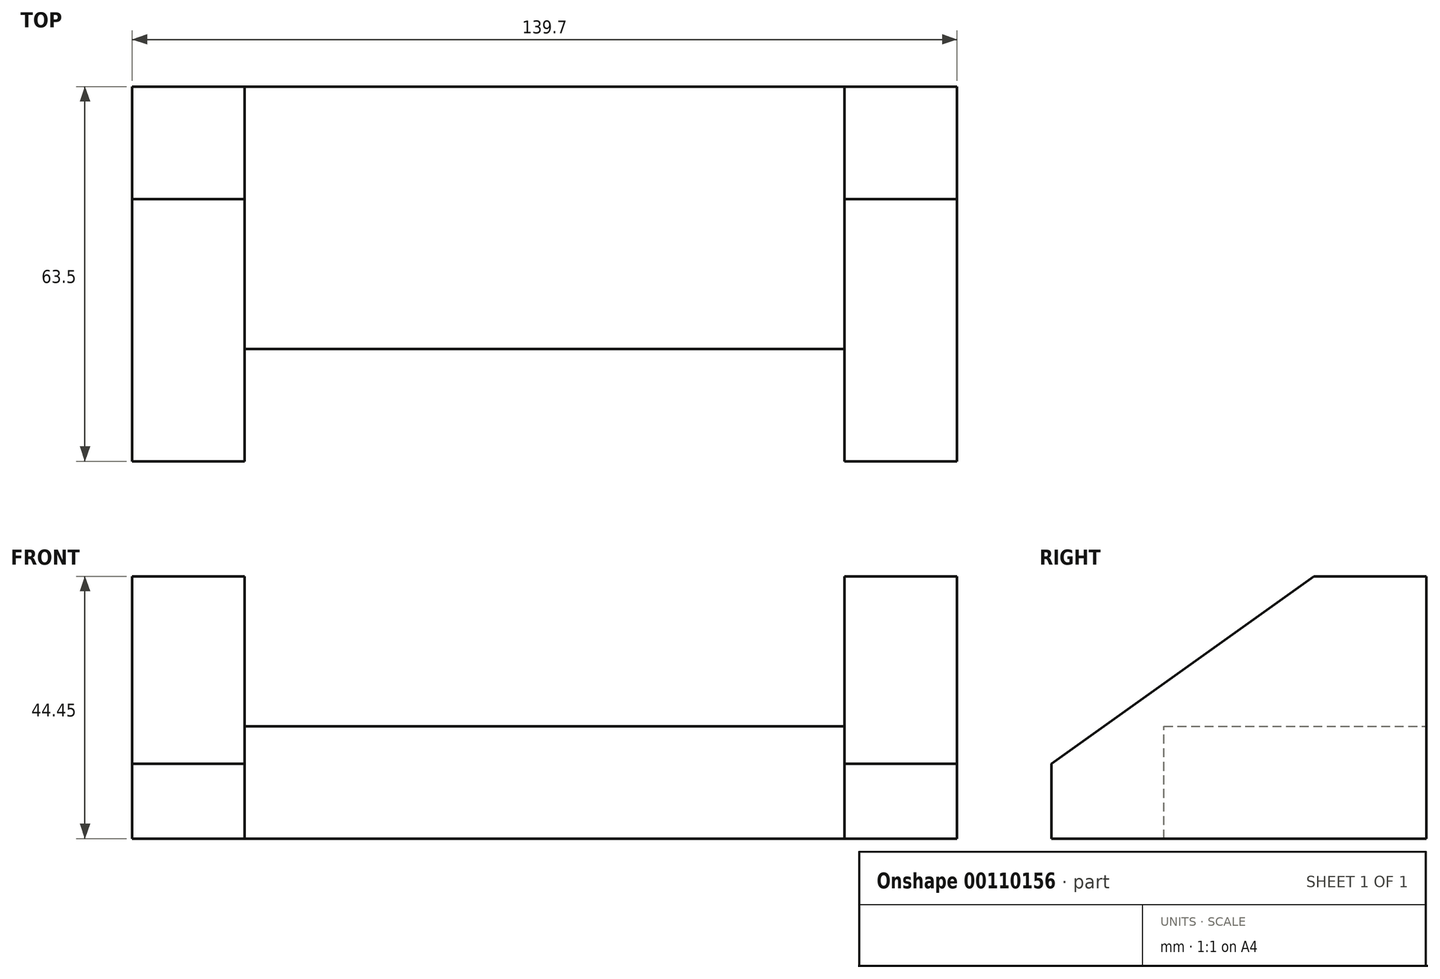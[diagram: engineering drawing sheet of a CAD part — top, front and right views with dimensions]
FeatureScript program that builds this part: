
annotation { "Feature Type Name" : "Feature", "Feature Type Description" : "" }
export const myFeature = defineFeature(function(context is Context, id is Id, definition is map)
    precondition{}
    {
        {
            var Q0;
            Q0=qCreatedBy(makeId("Right.planeOp"),FACE);
            var sketch = newSketch(context, id + "F0", { "sketchPlane" : qUnion([Q0])});
            skLineSegment(sketch, "E0", {"start": v(25.64, 0) * mm, "end": v(-37.86, 0) * mm});
            skLineSegment(sketch, "E1", {"start": v(-37.86, 0) * mm, "end": v(-37.86, 12.7) * mm});
            skLineSegment(sketch, "E2", {"start": v(25.64, 0) * mm, "end": v(25.64, 44.45) * mm});
            skLineSegment(sketch, "E3", {"start": v(-37.86, 12.7) * mm, "end": v(6.59, 44.45) * mm});
            skLineSegment(sketch, "E4", {"start": v(25.64, 44.45) * mm, "end": v(6.59, 44.45) * mm});
            skSolve(sketch);
        }
        {
            var Q0;
            Q0 = qSketchRegion(id + "F0", true);
            extrude(context, id + "F1", {"entities" : qUnion([Q0]), "depth" : 19.05 * mm});
        }
        {
            var Q0;
            Q0=makeQuery(id+"F1.opExtrude","CAP_FACE",FACE,{"disambiguationData":[OSD([sQuery(id+"F0.wireOp",EDGE,"E0"),sQuery(id+"F0.wireOp",EDGE,"E1"),sQuery(id+"F0.wireOp",EDGE,"E2"),sQuery(id+"F0.wireOp",EDGE,"E3"),sQuery(id+"F0.wireOp",EDGE,"E4")])],"isStart":false});
            var sketch = newSketch(context, id + "F2", { "sketchPlane" : qUnion([Q0])});
            skLineSegment(sketch, "E5", {"start": v(-18.81, 19.05) * mm, "end": v(25.64, 19.05) * mm});
            skLineSegment(sketch, "E6", {"start": v(25.64, 19.05) * mm, "end": v(25.64, 0) * mm});
            skLineSegment(sketch, "E7", {"start": v(25.64, 0) * mm, "end": v(-18.81, 0) * mm});
            skLineSegment(sketch, "E8", {"start": v(-18.81, 0) * mm, "end": v(-18.81, 19.05) * mm});
            skSolve(sketch);
        }
        {
            var Q0;
            Q0 = qSketchRegion(id + "F2", true);
            extrude(context, id + "F3", {"entities" : qUnion([Q0]), "depth" : 101.6 * mm});
        }
        {
            var Q0;
            Q0=makeQuery(id+"F3.opExtrude","CAP_FACE",FACE,{"disambiguationData":[OSD([sQuery(id+"F2.wireOp",EDGE,"E5"),sQuery(id+"F2.wireOp",EDGE,"E6"),sQuery(id+"F2.wireOp",EDGE,"E7"),sQuery(id+"F2.wireOp",EDGE,"E8")])],"isStart":false});
            var sketch = newSketch(context, id + "F4", { "sketchPlane" : qUnion([Q0])});
            skLineSegment(sketch, "E9", {"start": v(25.64, 0) * mm, "end": v(-37.86, 0) * mm});
            skLineSegment(sketch, "E10", {"start": v(-37.86, 0) * mm, "end": v(-37.86, 12.7) * mm});
            skLineSegment(sketch, "E11", {"start": v(6.59, 44.45) * mm, "end": v(-37.86, 12.7) * mm});
            skLineSegment(sketch, "E12", {"start": v(6.59, 44.45) * mm, "end": v(25.64, 44.45) * mm});
            skLineSegment(sketch, "E13", {"start": v(25.64, 44.45) * mm, "end": v(25.64, 0) * mm});
            skSolve(sketch);
        }
        {
            var Q0;
            Q0 = qSketchRegion(id + "F4", true);
            extrude(context, id + "F5", {"entities" : qUnion([Q0]), "depth" : 19.05 * mm});
        }
    });
